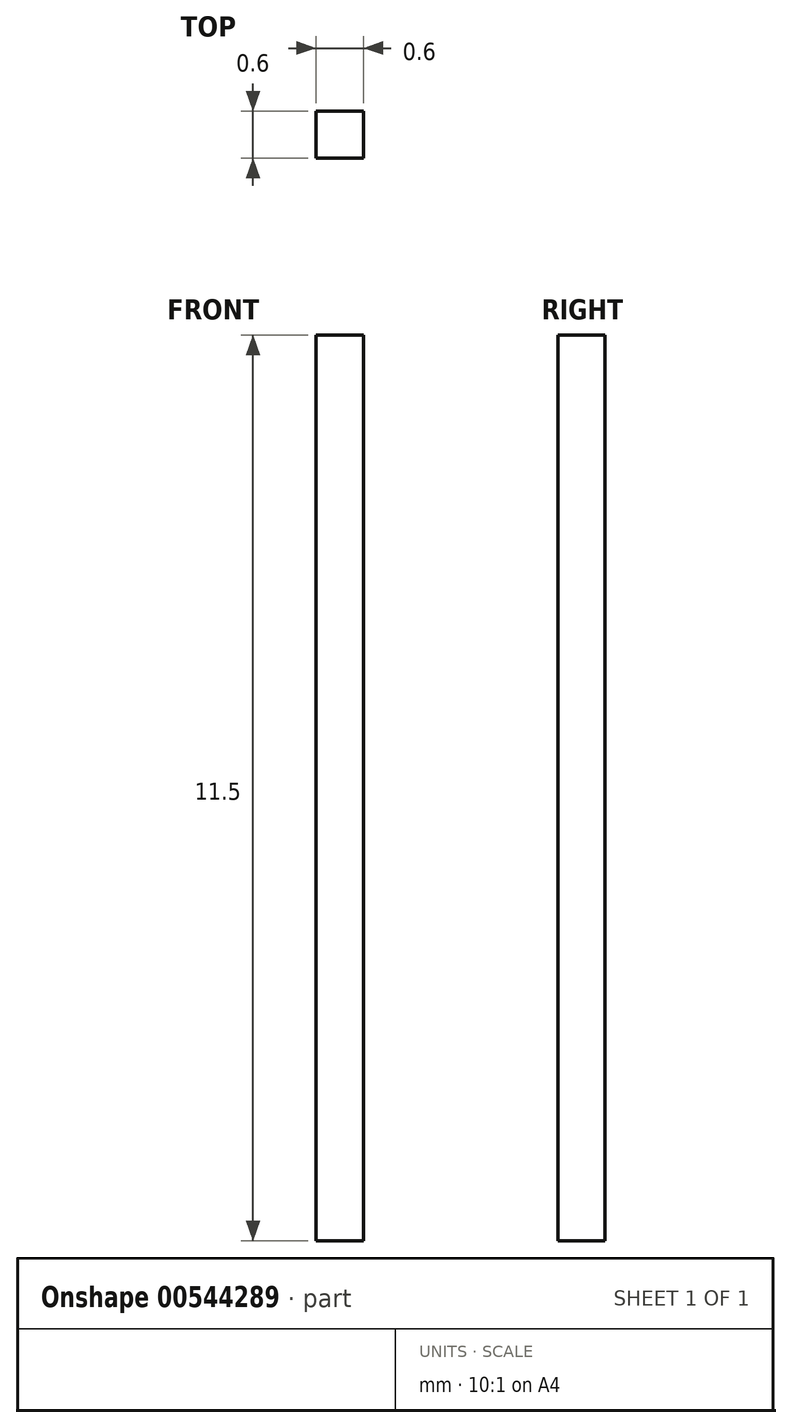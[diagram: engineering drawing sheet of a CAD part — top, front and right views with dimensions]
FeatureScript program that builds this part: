
annotation { "Feature Type Name" : "Feature", "Feature Type Description" : "" }
export const myFeature = defineFeature(function(context is Context, id is Id, definition is map)
    precondition{}
    {
        {
            var Q0;
            Q0=qCreatedBy(makeId("Top.planeOp"),FACE);
            var sketch = newSketch(context, id + "F0", { "sketchPlane" : qUnion([Q0])});
            skLineSegment(sketch, "E0.bottom", {"start": v(0, 0) * mm, "end": v(0.6, 0) * mm});
            skLineSegment(sketch, "E0.top", {"start": v(0, 0.6) * mm, "end": v(0.6, 0.6) * mm});
            skLineSegment(sketch, "E0.left", {"start": v(0, 0) * mm, "end": v(0, 0.6) * mm});
            skLineSegment(sketch, "E0.right", {"start": v(0.6, 0) * mm, "end": v(0.6, 0.6) * mm});
            skSolve(sketch);
        }
        {
            var Q0;
            Q0=qSketchRegion(id+"F0",true);
            extrude(context, id + "F1", {"entities" : qUnion([Q0]), "depth" : 11.5 * mm});
        }
    });
